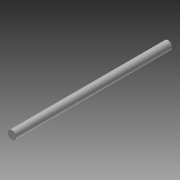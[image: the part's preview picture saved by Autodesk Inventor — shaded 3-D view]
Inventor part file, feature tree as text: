
AUTODESK INVENTOR PART (.ipt)
format: ipt  version: 2014 (Build 180170000, 170)  size: 68,096 bytes
history: native  units: in
note: dims shown in document units (in); Inventor stores cm internally (conversion verified against a paired STEP export)
features: extrude x1, sketch x1
ambient origin geometry x8: Origin, YZ Plane, XZ Plane, XY Plane, X Axis, Y Axis, Z Axis, Center Point
bodies: Solid1 (feature_tree)
feature tree (2):
  extrude  "Extrusion1"  Depth=7.0in TaperAngle=0.0deg
  sketch  "Sketch1"  dims[d0=0.375in d1=7.0in d2=0.0in]
